# Revit family: Sink-Undermount-Lavatory-KOHLER-Caxton_Round-K-29000_1
name_source: partatom
category: Plumbing Fixtures
units: mm (PartAtom-declared; Revit-internal decimal feet)

## family parameters
Cut with Voids When Loaded = No
Host = Face
Maintain Annotation Orientation = No
OmniClass Number = 23.31.13.00
OmniClass Title = Sinks
Part Type = Normal
Room Calculation Point = No
Round Connector Dimension = Use Diameter
Shared = No

## types (3) — shared parameters
ADA Compliant = Yes
Assembly Code = D2010400
CW Connection = No
Cold Water Inlet = Cold Water Inlet
Cutting Depth = 1"
Date Modified = 06/24/2022
Default Elevation = 36"
Description = Undercounter Lavatory
Drain Included = No
HW Connection = No
Height = 7 1/16"
Hot Water Inlet = Hot Water Inlet
Length = 16 1/8"
Manufacturer = Kohler Co.
Master Format 2014 = 22 41 16
Master Format 2014 Name = Residential Lavatories and Sinks
Material = Vitrious China
Product Documentation Link = https://www.us.kohler.com spec_US-CA_Kohler_en.pdf
Product Name = Caxton Round
Product Page URL = http://www.us.kohler.com
URL = https://www.us.kohler.com
Vent Connection = No
Waste Connection = Yes
Waste Water Outlet = Waste Water Outlet
WaterSense Certified = No
Width = 16 1/8"

## per-type parameters (varying)
| type | Finish | Model | Type |
| 0-White | Kohler-Vitreous_China-0-White | K-29000-0 | 1 |
| 7-Black Black | Kohler-Vitreous_China-7-Black_Black | K-29000-7 | 2 |
| 96-Biscuit | Kohler-Vitreous_China-96-Biscuit | K-29000-96 | 3 |

## geometry (parser evidence)
native form markers: Sweep x4
no freeform markers — native parametric forms only
